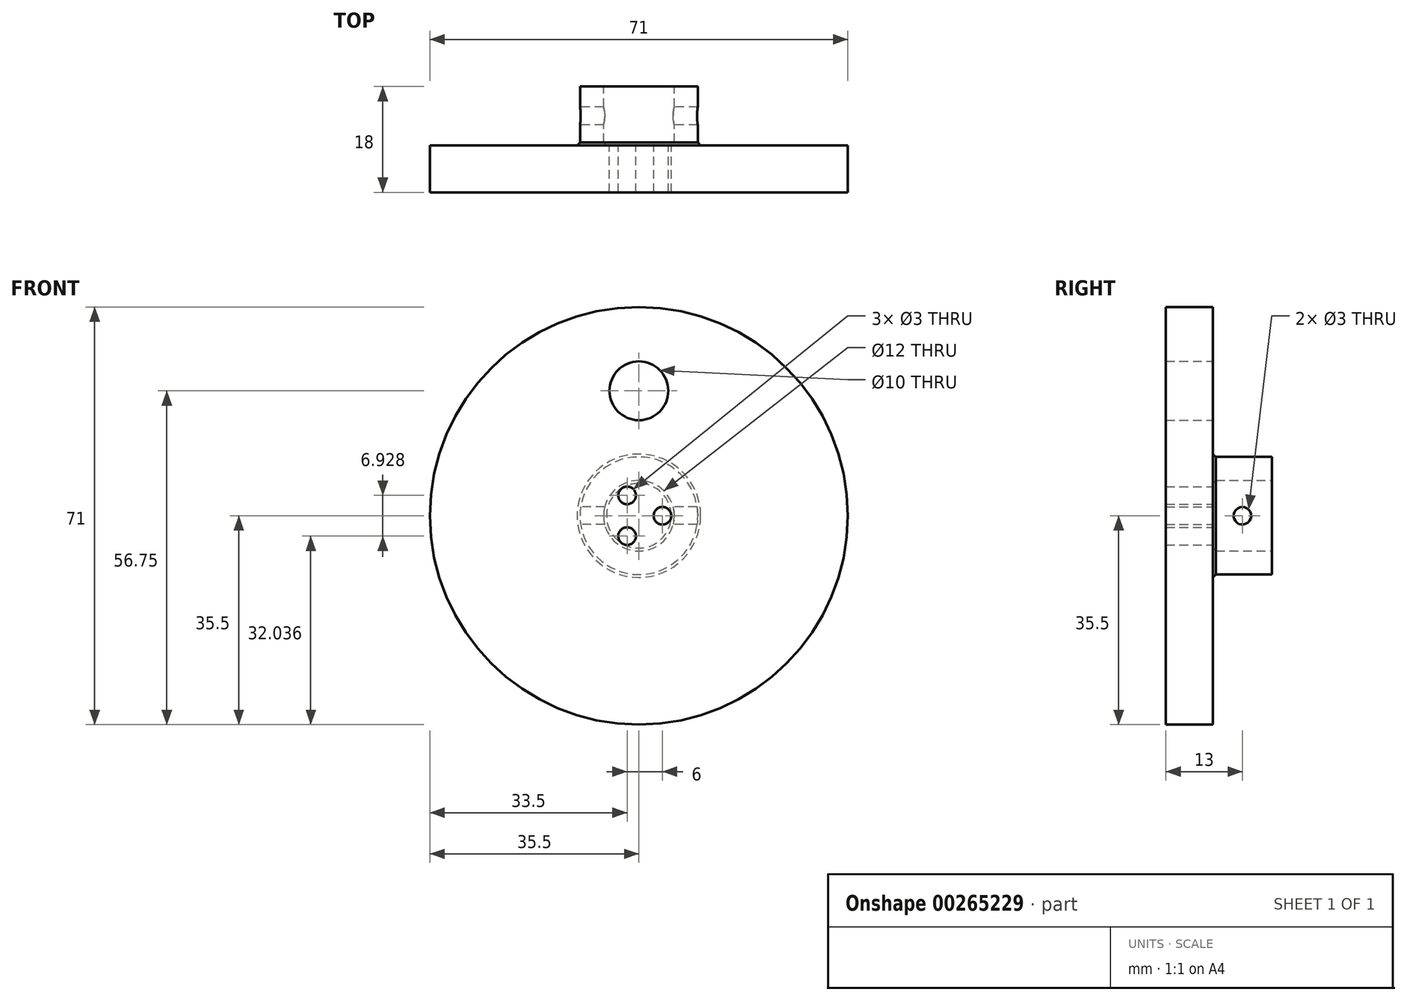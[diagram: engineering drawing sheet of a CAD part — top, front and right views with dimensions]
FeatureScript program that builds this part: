
annotation { "Feature Type Name" : "Feature", "Feature Type Description" : "" }
export const myFeature = defineFeature(function(context is Context, id is Id, definition is map)
    precondition{}
    {
        {
            var Q0;
            Q0=qCreatedBy(makeId("Front.planeOp"),FACE);
            var sketch = newSketch(context, id + "F0", { "sketchPlane" : qUnion([Q0])});
            skCircle(sketch, "E0", {"center": v(0, 0) * mm, "radius": 35.5 * mm});
            skSolve(sketch);
        }
        {
            var Q0;
            Q0=makeQuery(id+"F0.imprint","IMPRINT",FACE,{"disambiguationData":[TD([[makeQuery(id+"F0.imprint","IMPRINT",EDGE,{"derivedFrom":sQuery(id+"F0.wireOp",EDGE,"E0")}),1.0]])]});
            extrude(context, id + "F1", {"entities" : qUnion([Q0]), "depth" : 18 * mm});
        }
        {
            var Q0;
            Q0=makeQuery(id+"F1.opExtrude","CAP_FACE",FACE,{"disambiguationData":[OSD([sQuery(id+"F0.wireOp",EDGE,"E0")])],"isStart":true});
            var sketch = newSketch(context, id + "F2", { "sketchPlane" : qUnion([Q0])});
            skCircle(sketch, "E1", {"center": v(0, 0) * mm, "radius": 10 * mm});
            skCircle(sketch, "E2", {"center": v(0, 0) * mm, "radius": 65 * mm});
            skSolve(sketch);
        }
        {
            var Q0;
            Q0 = qSketchRegion(id + "F2", true);
            extrude(context, id + "F3", {"entities" : qUnion([Q0]), "operationType" : NewBodyOperationType.REMOVE, "oppositeDirection" : true, "depth" : 10 * mm});
        }
        {
            var Q0;
            Q0=makeQuery(id+"F1.opExtrude","CAP_FACE",FACE,{"disambiguationData":[OSD([sQuery(id+"F0.wireOp",EDGE,"E0")])],"isStart":true});
            var sketch = newSketch(context, id + "F4", { "sketchPlane" : qUnion([Q0])});
            skCircle(sketch, "E3", {"center": v(0, 0) * mm, "radius": 6 * mm});
            skSolve(sketch);
        }
        {
            var Q0;
            Q0=makeQuery(id+"F4.imprint","IMPRINT",FACE,{"disambiguationData":[TD([[makeQuery(id+"F4.imprint","IMPRINT",EDGE,{"derivedFrom":sQuery(id+"F4.wireOp",EDGE,"E3")}),1.0]])]});
            extrude(context, id + "F5", {"entities" : qUnion([Q0]), "operationType" : NewBodyOperationType.REMOVE, "oppositeDirection" : true, "depth" : 10 * mm});
        }
        {
            var Q0;
            Q0=makeQuery(id+"F3.boolean.opBoolean","COPY",EDGE,{"derivedFrom":makeQuery(id+"F3.opExtrude","CAP_EDGE",EDGE,{"disambiguationData":[OSD([sQuery(id+"F2.wireOp",EDGE,"E1")])],"isStart":false})});
            chamfer(context, id + "F6", {"entities" : qUnion([Q0]), "width" : .5 * mm, "tangentPropagation" : true});
        }
        {
            var Q0;
            Q0=qCreatedBy(makeId("Right.planeOp"),FACE);
            var sketch = newSketch(context, id + "F7", { "sketchPlane" : qUnion([Q0])});
            skPoint(sketch, "E4", {"position": v(-5, 0) * mm});
            skCircle(sketch, "E5", {"center": v(-5, 0) * mm, "radius": 1.5 * mm});
            skSolve(sketch);
        }
        {
            var Q0;
            Q0 = qSketchRegion(id + "F7", true);
            extrude(context, id + "F8", {"entities" : qUnion([Q0]), "operationType" : NewBodyOperationType.REMOVE, "depth" : 25 * mm, "hasSecondDirection" : true, "secondDirectionOppositeDirection" : true, "secondDirectionDepth" : 25 * mm});
        }
        {
            var Q0;
            Q0=qCreatedBy(makeId("Front.planeOp"),FACE);
            var sketch = newSketch(context, id + "F9", { "sketchPlane" : qUnion([Q0])});
            skPoint(sketch, "E6", {"position": v(0, 0) * mm});
            skPoint(sketch, "E7", {"position": v(0, 21.25) * mm});
            skCircle(sketch, "E8", {"center": v(0, 21.25) * mm, "radius": 5 * mm});
            skSolve(sketch);
        }
        {
            var Q0;
            Q0 = qSketchRegion(id + "F9", true);
            extrude(context, id + "F10", {"entities" : qUnion([Q0]), "operationType" : NewBodyOperationType.REMOVE, "depth" : 25 * mm});
        }
        {
            var Q0;
            Q0=makeQuery(id+"F5.boolean.opBoolean","COPY",EDGE,{"derivedFrom":makeQuery(id+"F5.opExtrude","CAP_EDGE",EDGE,{"disambiguationData":[OSD([sQuery(id+"F4.wireOp",EDGE,"E3")])],"isStart":false})});
            chamfer(context, id + "F11", {"entities" : qUnion([Q0]), "width" : .5 * mm, "tangentPropagation" : true});
        }
        {
            var Q0;
            Q0=qCreatedBy(makeId("Front.planeOp"),FACE);
            var sketch = newSketch(context, id + "F12", { "sketchPlane" : qUnion([Q0])});
            skCircle(sketch, "E9.cCircle", {"center": v(0, 0) * mm, "radius": 2 * mm, "construction": true});
            skLineSegment(sketch, "E9.0", {"start": v(-2, -3.46) * mm, "end": v(-2, 3.46) * mm, "construction": true});
            skLineSegment(sketch, "E9.1", {"start": v(-2, 3.46) * mm, "end": v(4, 0) * mm, "construction": true});
            skLineSegment(sketch, "E9.2", {"start": v(4, 0) * mm, "end": v(-2, -3.46) * mm, "construction": true});
            skPoint(sketch, "E9.0.midPoint", {"position": v(-2, 0) * mm});
            skCircle(sketch, "E10", {"center": v(-2, 3.46) * mm, "radius": 1.5 * mm});
            skCircle(sketch, "E11", {"center": v(-2, -3.46) * mm, "radius": 1.5 * mm});
            skCircle(sketch, "E12", {"center": v(4, 0) * mm, "radius": 1.5 * mm});
            skSolve(sketch);
        }
        {
            var Q0;
            Q0 = qSketchRegion(id + "F12", true);
            extrude(context, id + "F13", {"entities" : qUnion([Q0]), "operationType" : NewBodyOperationType.REMOVE, "depth" : 20 * mm});
        }
    });
